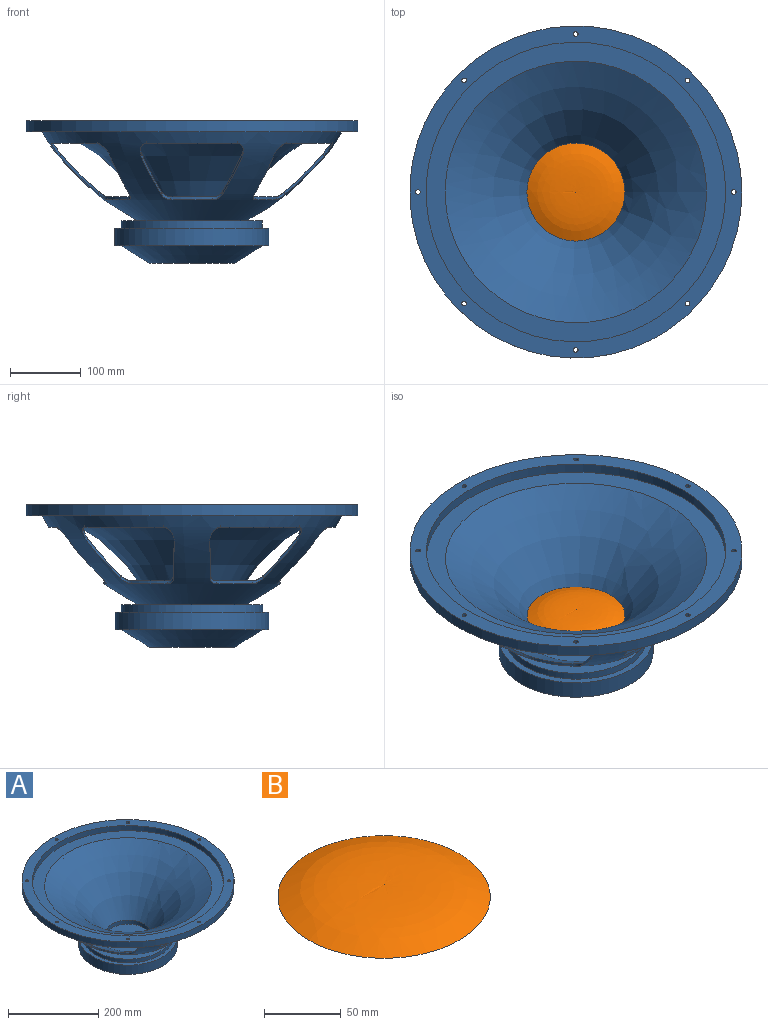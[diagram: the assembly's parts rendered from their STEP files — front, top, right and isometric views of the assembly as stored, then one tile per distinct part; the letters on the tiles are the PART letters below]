
ASSEMBLY  parts=2 mates=1
PART A: 79 faces, bbox 470x470x202 mm
  f0: plane 414.06x414.06mm, normal (0,0,-1), area 31591.5mm2, adj f1,f3
  f1: revolved ~414.06x414.06mm, area 85776.7mm2, adj f0,f2,f4,f5,f6,f7,f8,f9
  f2: plane 146.35x146.35mm, normal (0,0,1), area 7892.5mm2, adj f1,f3
  f3: revolved ~362.24x362.24mm, area 125335mm2, adj f0,f2
  f4: cylinder r=12.5mm len=25.67mm, axis (0,0,-1), area 134.8mm2, adj f1,f5,f8,f68
  f5: cylinder r=202.5mm len=128.73mm, axis (0,0,-1), area 822.5mm2, adj f1,f4,f6,f68
  f6: cylinder r=12.5mm len=25.67mm, axis (0,0,-1), area 134.8mm2, adj f1,f5,f9,f68
  f7: cylinder r=12.5mm len=13.69mm, axis (0,0,-1), area 68.5mm2, adj f1,f8,f11,f68
  f8: plane 58.63x46.64mm, normal (0.86,0.51,0), area 260.4mm2, adj f1,f4,f7,f68
  f9: plane 58.63x46.64mm, normal (-0.86,0.51,0), area 260.4mm2, adj f1,f6,f10,f68
  f10: cylinder r=12.5mm len=13.69mm, axis (0,0,-1), area 68.5mm2, adj f1,f9,f11,f68
  f11: cylinder r=124.91mm len=59.12mm, axis (0,0,-1), area 253.3mm2, adj f1,f7,f10,f68
  f12: cylinder r=12.5mm len=25.67mm, axis (0,0,-1), area 134.8mm2, adj f1,f13,f16,f68
  f13: cylinder r=202.5mm len=111.49mm, axis (0,0,-1), area 822.5mm2, adj f1,f12,f14,f68
  f14: cylinder r=12.5mm len=25.67mm, axis (0,0,-1), area 134.8mm2, adj f1,f13,f17,f68
  f15: cylinder r=12.5mm len=11.84mm, axis (0,0,-1), area 68.5mm2, adj f1,f16,f19,f68
  f16: plane 58.63x54.33mm, normal (-0.02,1,0), area 260.4mm2, adj f1,f12,f15,f68
  f17: plane 58.63x47.46mm, normal (-0.87,-0.49,0), area 260.4mm2, adj f1,f14,f18,f68
  f18: cylinder r=12.5mm len=14.72mm, axis (0,0,-1), area 68.5mm2, adj f1,f17,f19,f68
  f19: cylinder r=124.91mm len=51.2mm, axis (0,0,-1), area 253.3mm2, adj f1,f15,f18,f68
  f20: cylinder r=12.5mm len=25.67mm, axis (0,0,-1), area 134.8mm2, adj f1,f21,f24,f68
  f21: cylinder r=202.5mm len=111.49mm, axis (0,0,-1), area 822.5mm2, adj f1,f20,f22,f68
  f22: cylinder r=12.5mm len=25.67mm, axis (0,0,-1), area 134.8mm2, adj f1,f21,f25,f68
  f23: cylinder r=12.5mm len=11.84mm, axis (0,0,-1), area 68.5mm2, adj f1,f24,f27,f68
  f24: plane 58.63x54.33mm, normal (0.02,-1,0), area 260.4mm2, adj f1,f20,f23,f68
  f25: plane 58.63x47.46mm, normal (0.87,0.49,0), area 260.4mm2, adj f1,f22,f26,f68
  f26: cylinder r=12.5mm len=14.72mm, axis (0,0,-1), area 68.5mm2, adj f1,f25,f27,f68
  f27: cylinder r=124.91mm len=51.2mm, axis (0,0,-1), area 253.3mm2, adj f1,f23,f26,f68
  f28: cylinder r=12.5mm len=25.67mm, axis (0,0,-1), area 134.8mm2, adj f1,f29,f32,f68
  f29: cylinder r=202.5mm len=111.49mm, axis (0,0,-1), area 822.5mm2, adj f1,f28,f30,f68
  f30: cylinder r=12.5mm len=25.67mm, axis (0,0,-1), area 134.8mm2, adj f1,f29,f33,f68
  f31: cylinder r=12.5mm len=14.72mm, axis (0,0,-1), area 68.5mm2, adj f1,f32,f35,f68
  f32: plane 58.63x47.46mm, normal (0.87,-0.49,0), area 260.4mm2, adj f1,f28,f31,f68
  f33: plane 58.63x54.33mm, normal (0.02,1,0), area 260.4mm2, adj f1,f30,f34,f68
  f34: cylinder r=12.5mm len=11.84mm, axis (0,0,-1), area 68.5mm2, adj f1,f33,f35,f68
  f35: cylinder r=124.91mm len=51.2mm, axis (0,0,-1), area 253.3mm2, adj f1,f31,f34,f68
  f36: cylinder r=12.5mm len=25.67mm, axis (0,0,-1), area 134.8mm2, adj f1,f37,f40,f68
  f37: cylinder r=202.5mm len=111.49mm, axis (0,0,-1), area 822.5mm2, adj f1,f36,f38,f68
  f38: cylinder r=12.5mm len=25.67mm, axis (0,0,-1), area 134.8mm2, adj f1,f37,f41,f68
  f39: cylinder r=12.5mm len=14.72mm, axis (0,0,-1), area 68.5mm2, adj f1,f40,f43,f68
  f40: plane 58.63x47.46mm, normal (-0.87,0.49,0), area 260.4mm2, adj f1,f36,f39,f68
  f41: plane 58.63x54.33mm, normal (-0.02,-1,0), area 260.4mm2, adj f1,f38,f42,f68
  f42: cylinder r=12.5mm len=11.84mm, axis (0,0,-1), area 68.5mm2, adj f1,f41,f43,f68
  f43: cylinder r=124.91mm len=51.2mm, axis (0,0,-1), area 253.3mm2, adj f1,f39,f42,f68
  f44: cylinder r=12.5mm len=25.67mm, axis (0,0,-1), area 134.8mm2, adj f1,f45,f48,f68
  f45: cylinder r=202.5mm len=128.73mm, axis (0,0,-1), area 822.5mm2, adj f1,f44,f46,f68
  f46: cylinder r=12.5mm len=25.67mm, axis (0,0,-1), area 134.8mm2, adj f1,f45,f49,f68
  f47: cylinder r=12.5mm len=13.69mm, axis (0,0,-1), area 68.5mm2, adj f1,f48,f51,f68
  f48: plane 58.63x46.64mm, normal (-0.86,-0.51,0), area 260.4mm2, adj f1,f44,f47,f68
  f49: plane 58.63x46.64mm, normal (0.86,-0.51,0), area 260.4mm2, adj f1,f46,f50,f68
  f50: cylinder r=12.5mm len=13.69mm, axis (0,0,-1), area 68.5mm2, adj f1,f49,f51,f68
  f51: cylinder r=124.91mm len=59.12mm, axis (0,0,-1), area 253.3mm2, adj f1,f47,f50,f68
  f52: plane 108x108mm, normal (0,0,-1), area 1306.9mm2, adj f56,f57
  f53: plane 98x98mm, normal (0,0,1), area 7543mm2, adj f54
  f54: cylinder r=49mm len=98mm, axis (0,0,-1), area 12315mm2, adj f53,f55
  f55: plane 108x108mm, normal (0,0,1), area 1617.9mm2, adj f54,f56
  f56: cylinder r=54mm len=108mm, axis (0,0,-1), area 16964.6mm2, adj f52,f55
  f57: revolved ~370x370mm, area 131660.5mm2, adj f52,f70
  f58: cylinder r=100mm len=200mm, axis (0,0,-1), area 6283.2mm2, adj f59,f60
  f59: plane 200x200mm, normal (0,0,1), area 13095.2mm2, adj f58,f68
  f60: plane 218x218mm, normal (0,0,1), area 5909.3mm2, adj f58,f62
  f61: plane 218x218mm, normal (0,0,-1), area 5909.3mm2, adj f62,f64
  f62: cylinder r=109mm len=218mm, axis (0,0,-1), area 17121.7mm2, adj f60,f61
  f63: plane 120x120mm, normal (0,0,-1), area 11309.7mm2, adj f64
  f64: cone r=60mm half-angle=58deg, axis (0,0,1), area 23710.2mm2, adj f61,f63
  f65: plane 470x470mm, normal (0,0,1), area 32033.2mm2, adj f66,f69,f71,f72,f73,f74,f75,f76
  f66: cylinder r=235mm len=470mm, axis (0,0,1), area 23624.8mm2, adj f65,f67
  f67: plane 470x470mm, normal (0,0,-1), area 32033.2mm2, adj f66,f68,f71,f72,f73,f74,f75,f76
  f68: revolved ~424x424mm, area 96511.7mm2, adj f4,f5,f6,f7,f8,f9,f10,f11
  f69: cylinder r=212mm len=424mm, axis (0,0,1), area 18648.5mm2, adj f65,f70
  f70: plane 424x424mm, normal (0,0,1), area 33674.7mm2, adj f57,f69
  f71: cylinder r=3.25mm len=16mm, axis (0,0,1), area 326.7mm2, adj f65,f67
  f72: cylinder r=3.25mm len=16mm, axis (0,0,1), area 326.7mm2, adj f65,f67
  f73: cylinder r=3.25mm len=16mm, axis (0,0,1), area 326.7mm2, adj f65,f67
  f74: cylinder r=3.25mm len=16mm, axis (0,0,1), area 326.7mm2, adj f65,f67
  f75: cylinder r=3.25mm len=16mm, axis (0,0,1), area 326.7mm2, adj f65,f67
  f76: cylinder r=3.25mm len=16mm, axis (0,0,1), area 326.7mm2, adj f65,f67
  f77: cylinder r=3.25mm len=16mm, axis (0,0,1), area 326.7mm2, adj f65,f67
  f78: cylinder r=3.25mm len=16mm, axis (0,0,1), area 326.7mm2, adj f65,f67
PART B: 2 faces, bbox 138.6x138.6x10.1 mm
  f0: revolved ~138.61x138.61mm, area 15637.4mm2, adj f1
  f1: plane 138.61x138.61mm, normal (0,0,-1), area 15089.2mm2, adj f0
PLACE A at identity
PLACE B at identity
MATE fastened B.f1 <-> A.f54  axis (0,0,1) through (0,0,90)mm
